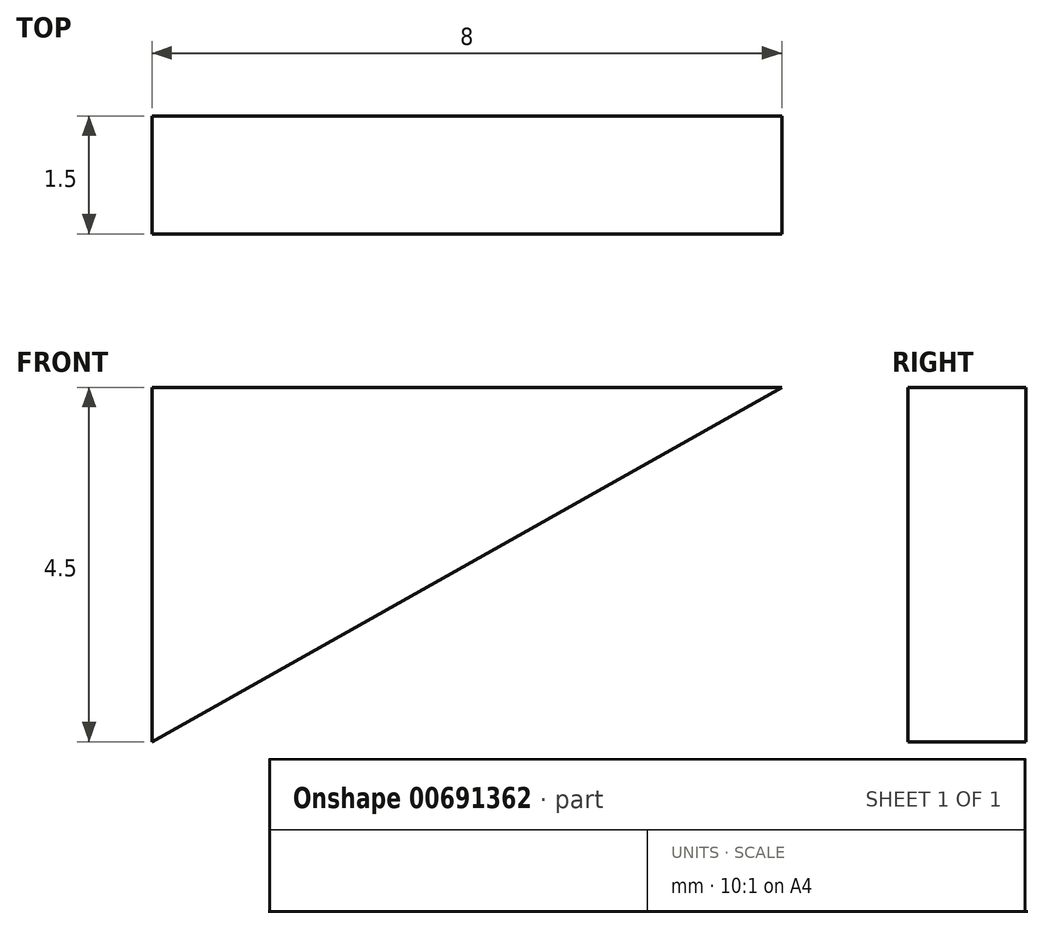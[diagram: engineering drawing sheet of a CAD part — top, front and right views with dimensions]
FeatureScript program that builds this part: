
annotation { "Feature Type Name" : "Feature", "Feature Type Description" : "" }
export const myFeature = defineFeature(function(context is Context, id is Id, definition is map)
    precondition{}
    {
        {
            var Q0;
            Q0=qCreatedBy(makeId("Front.planeOp"),FACE);
            var sketch = newSketch(context, id + "F0", { "sketchPlane" : qUnion([Q0])});
            skLineSegment(sketch, "E0", {"start": v(0, 0) * mm, "end": v(0, 4.5) * mm});
            skLineSegment(sketch, "E1", {"start": v(0, 4.5) * mm, "end": v(8, 4.5) * mm});
            skLineSegment(sketch, "E2", {"start": v(8, 4.5) * mm, "end": v(0, 0) * mm});
            skSolve(sketch);
        }
        {
            var Q0;
            Q0 = qSketchRegion(id + "F0", true);
            extrude(context, id + "F1", {"entities" : qUnion([Q0]), "depth" : 1.5 * mm, "offsetDistance" : 25 * mm});
        }
    });
